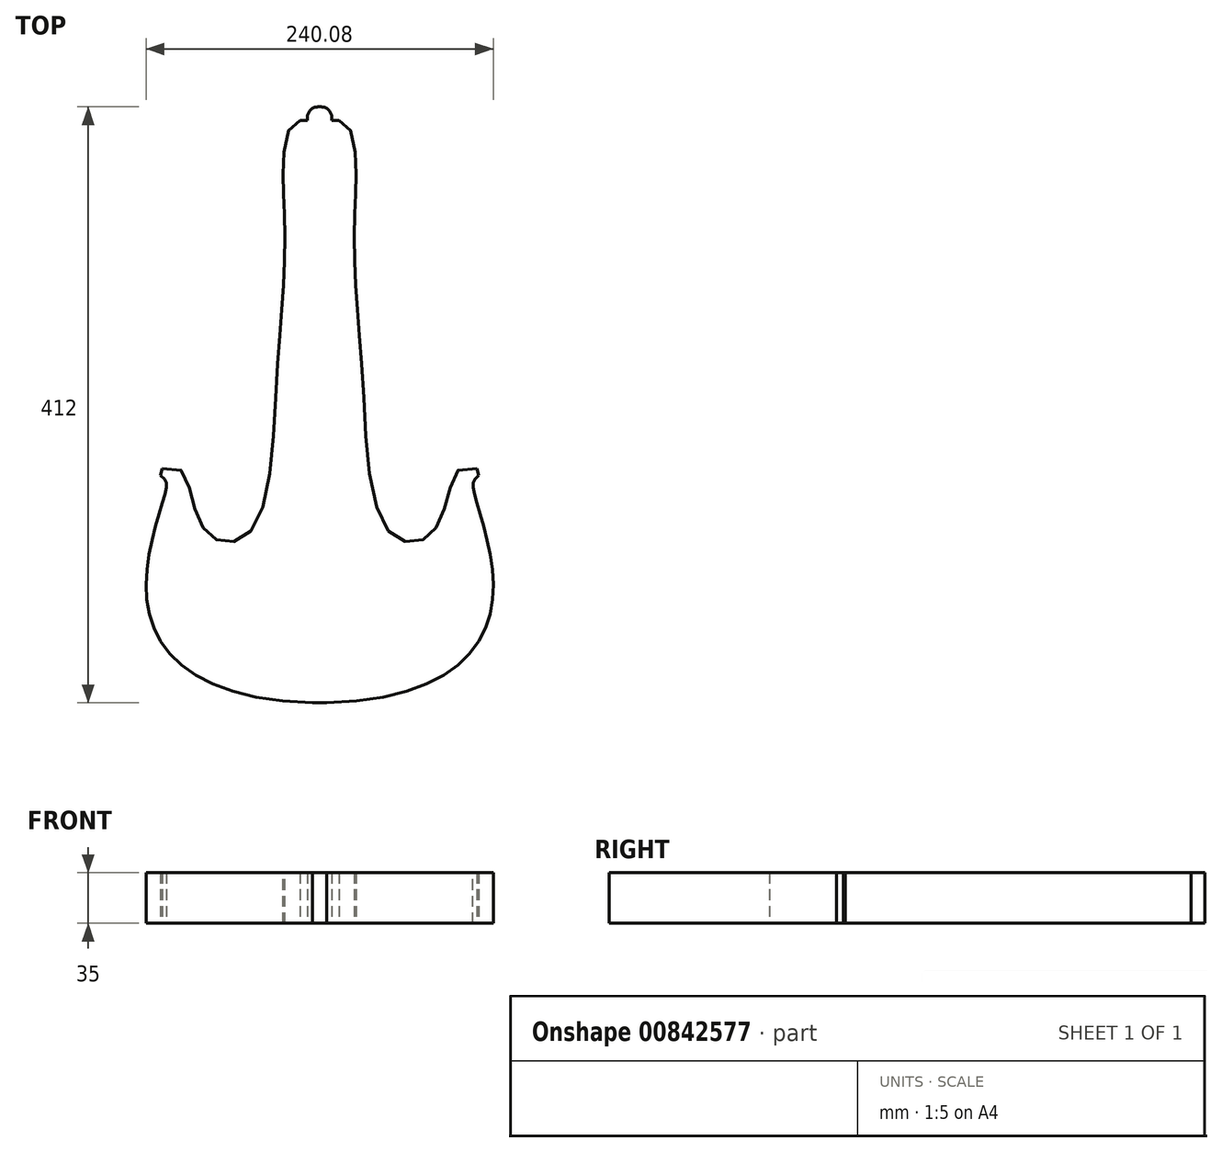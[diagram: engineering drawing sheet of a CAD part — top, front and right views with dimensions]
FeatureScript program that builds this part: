
annotation { "Feature Type Name" : "Feature", "Feature Type Description" : "" }
export const myFeature = defineFeature(function(context is Context, id is Id, definition is map)
    precondition{}
    {
        {
            var Q0;
            Q0=qCreatedBy(makeId("Top.planeOp"),FACE);
            var sketch = newSketch(context, id + "F0", { "sketchPlane" : qUnion([Q0])});
            skLineSegment(sketch, "E0", {"start": v(0, 292.22) * mm, "end": v(-1, 292.22) * mm});
            skLineSegment(sketch, "E1", {"start": v(-1, 292.22) * mm, "end": v(-1, -119.78) * mm});
            skLineSegment(sketch, "E2", {"start": v(12.5, 282.72) * mm, "end": v(7.5, 282.72) * mm});
            skLineSegment(sketch, "E3", {"start": v(7.5, 282.72) * mm, "end": v(7.5, 284.72) * mm});
            skArc(sketch, "E4", {"start": v(7.5, 284.72) * mm, "mid": v(5.3, 290.03) * mm, "end": v(0, 292.22) * mm});
            skFitSpline(sketch, "E5", {"points": [v(94, 207.22) * mm, v(85.5, 153.22) * mm, v(90.5, 141.22) * mm], "startDerivative": vector(-1.32, -59.7) * mm, "endDerivative": vector(44.59, -33.71) * mm, "construction": true});
            skLineSegment(sketch, "E6", {"start": v(90.5, 141.22) * mm, "end": v(89.1, 136.42) * mm, "construction": true});
            skFitSpline(sketch, "E7", {"points": [v(89.1, 136.42) * mm, v(62, 106.22) * mm], "startDerivative": vector(-47.74, 16.25) * mm, "endDerivative": vector(0.93, -57.04) * mm, "construction": true});
            skFitSpline(sketch, "E8", {"points": [v(62, 106.22) * mm, v(107.7, 42.22) * mm], "startDerivative": vector(-1.92, -75.42) * mm, "endDerivative": vector(57.85, 84.17) * mm, "construction": true});
            skLineSegment(sketch, "E9", {"start": v(107.7, 42.22) * mm, "end": v(109, 37.4) * mm});
            skFitSpline(sketch, "E10", {"points": [v(109, 37.4) * mm, v(105, 29.4) * mm, v(119, -41.78) * mm, v(4, -119.78) * mm], "startDerivative": vector(-78.73, -70.42) * mm, "endDerivative": vector(-504.13, -13.55) * mm});
            skLineSegment(sketch, "E11", {"start": v(-1, -119.78) * mm, "end": v(4, -119.78) * mm});
            skFitSpline(sketch, "E12", {"points": [v(94, 207.22) * mm, v(12.5, 282.72) * mm], "startDerivative": vector(2.52, 114) * mm, "endDerivative": vector(-185.72, -1.91) * mm, "construction": true});
            skFitSpline(sketch, "E13", {"points": [v(107.7, 42.22) * mm, v(88.6, 26.72) * mm, v(73.3, -5.53) * mm, v(46.77, -1.32) * mm, v(29, 100.22) * mm, v(24, 167.27) * mm, v(23.33, 217.81) * mm, v(24, 255.34) * mm, v(12.5, 282.72) * mm], "startDerivative": vector(-438.12, 161.47) * mm, "endDerivative": vector(-250.96, 4.95) * mm});
            skLineSegment(sketch, "E14", {"start": v(75.99, 56.87) * mm, "end": v(-1, 56.87) * mm, "construction": true});
            skLineSegment(sketch, "E15", {"start": v(119, -41.78) * mm, "end": v(119, 290) * mm, "construction": true});
            skSolve(sketch);
        }
        {
            var Q0;
            Q0=qSketchRegion(id+"F0",true);
            extrude(context, id + "F1", {"entities" : qUnion([Q0]), "depth" : 35 * mm});
        }
        {
            var Q0;
            Q0=makeQuery(id+"F1.opExtrude","SWEPT_BODY",BODY,{"disambiguationData":[OSD([sQuery(id+"F0.wireOp",EDGE,"E0"),sQuery(id+"F0.wireOp",EDGE,"E1"),sQuery(id+"F0.wireOp",EDGE,"E2"),sQuery(id+"F0.wireOp",EDGE,"E3"),sQuery(id+"F0.wireOp",EDGE,"E4"),sQuery(id+"F0.wireOp",EDGE,"E5"),sQuery(id+"F0.wireOp",EDGE,"E6"),sQuery(id+"F0.wireOp",EDGE,"E7"),sQuery(id+"F0.wireOp",EDGE,"E8"),sQuery(id+"F0.wireOp",EDGE,"E9"),sQuery(id+"F0.wireOp",EDGE,"E10"),sQuery(id+"F0.wireOp",EDGE,"E11"),sQuery(id+"F0.wireOp",EDGE,"E12")])]});
            var Q1;
            Q1=makeQuery(id+"F1.opExtrude","SWEPT_FACE",FACE,{"disambiguationData":[OSD([sQuery(id+"F0.wireOp",EDGE,"E1")])]});
            mirror(context, id + "F2", {"operationType" : NewBodyOperationType.ADD, "entities" : qUnion([Q0]), "mirrorPlane" : qUnion([Q1])});
        }
    });
